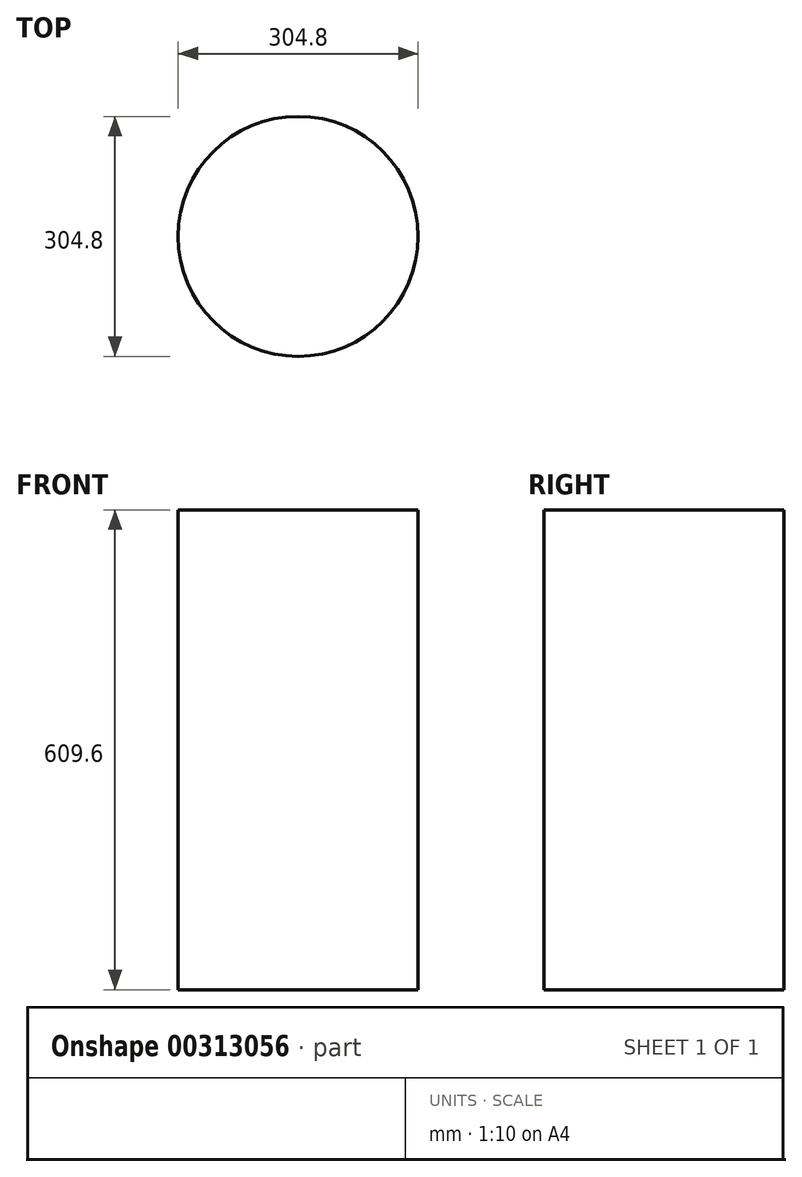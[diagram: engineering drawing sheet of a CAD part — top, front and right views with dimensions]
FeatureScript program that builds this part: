
annotation { "Feature Type Name" : "Feature", "Feature Type Description" : "" }
export const myFeature = defineFeature(function(context is Context, id is Id, definition is map)
    precondition{}
    {
        {
            var Q0;
            Q0=qCreatedBy(makeId("Top.planeOp"),FACE);
            var sketch = newSketch(context, id + "F0", { "sketchPlane" : qUnion([Q0])});
            skCircle(sketch, "E0", {"center": v(-46.78, 35.51) * mm, "radius": 152.4 * mm});
            skSolve(sketch);
        }
        {
            var Q0;
            Q0=makeQuery(id+"F0.imprint","IMPRINT",FACE,{"disambiguationData":[TD([[makeQuery(id+"F0.imprint","IMPRINT",EDGE,{"derivedFrom":sQuery(id+"F0.wireOp",EDGE,"E0")}),1.0]])]});
            extrude(context, id + "F1", {"entities" : qUnion([Q0]), "depth" : 609.6 * mm});
        }
    });
